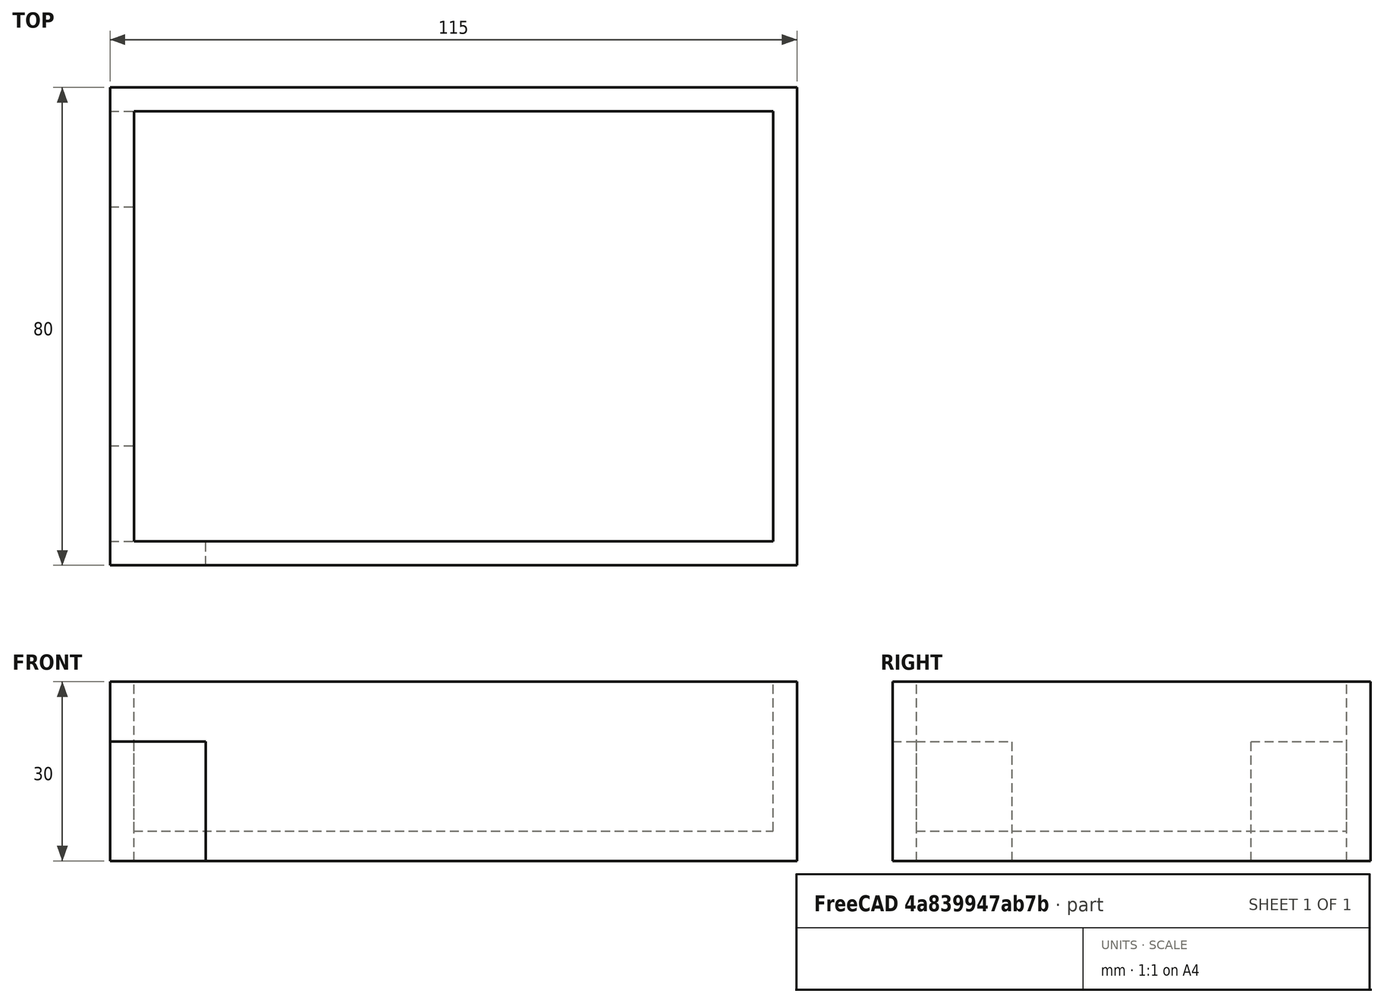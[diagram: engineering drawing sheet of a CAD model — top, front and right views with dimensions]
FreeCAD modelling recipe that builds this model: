
FCSTD DOCUMENT  (FreeCAD 0.18R4 (GitTag))
Label: Gehause
License: All rights reserved
LicenseURL: http://en.wikipedia.org/wiki/All_rights_reserved
objects: Part::Box×5
note: 5 computed .brp shape members not serialized (recipe doc carries the construction recipe); baked Part::Feature solids carry a one-line shape summary decoded from their .brp

FEATURE [Part::Box] Box  label="Basis"
  AttacherType = Attacher::AttachEngine3D
  Height = 30
  Length = 115
  Width = 80
FEATURE [Part::Box] Box001  label="Basis_Cut"
  AttacherType = Attacher::AttachEngine3D
  Height = 25
  Length = 107
  Placement = pos=(4,4,5) rot=(0,0,1;0rad)
  Width = 72
FEATURE [Part::Box] Box002  label="Solar"
  AttacherType = Attacher::AttachEngine3D
  Height = 20
  Length = 4
  Placement = pos=(0,4,0) rot=(0,0,1;0rad)
  Width = 16
FEATURE [Part::Box] Box003  label="Antenne"
  AttacherType = Attacher::AttachEngine3D
  Height = 20
  Length = 4
  Placement = pos=(0,60,0) rot=(0,0,1;0rad)
  Width = 16
FEATURE [Part::Box] Box004  label="Luftsensor"
  AttacherType = Attacher::AttachEngine3D
  Height = 20
  Length = 16
  Width = 4
